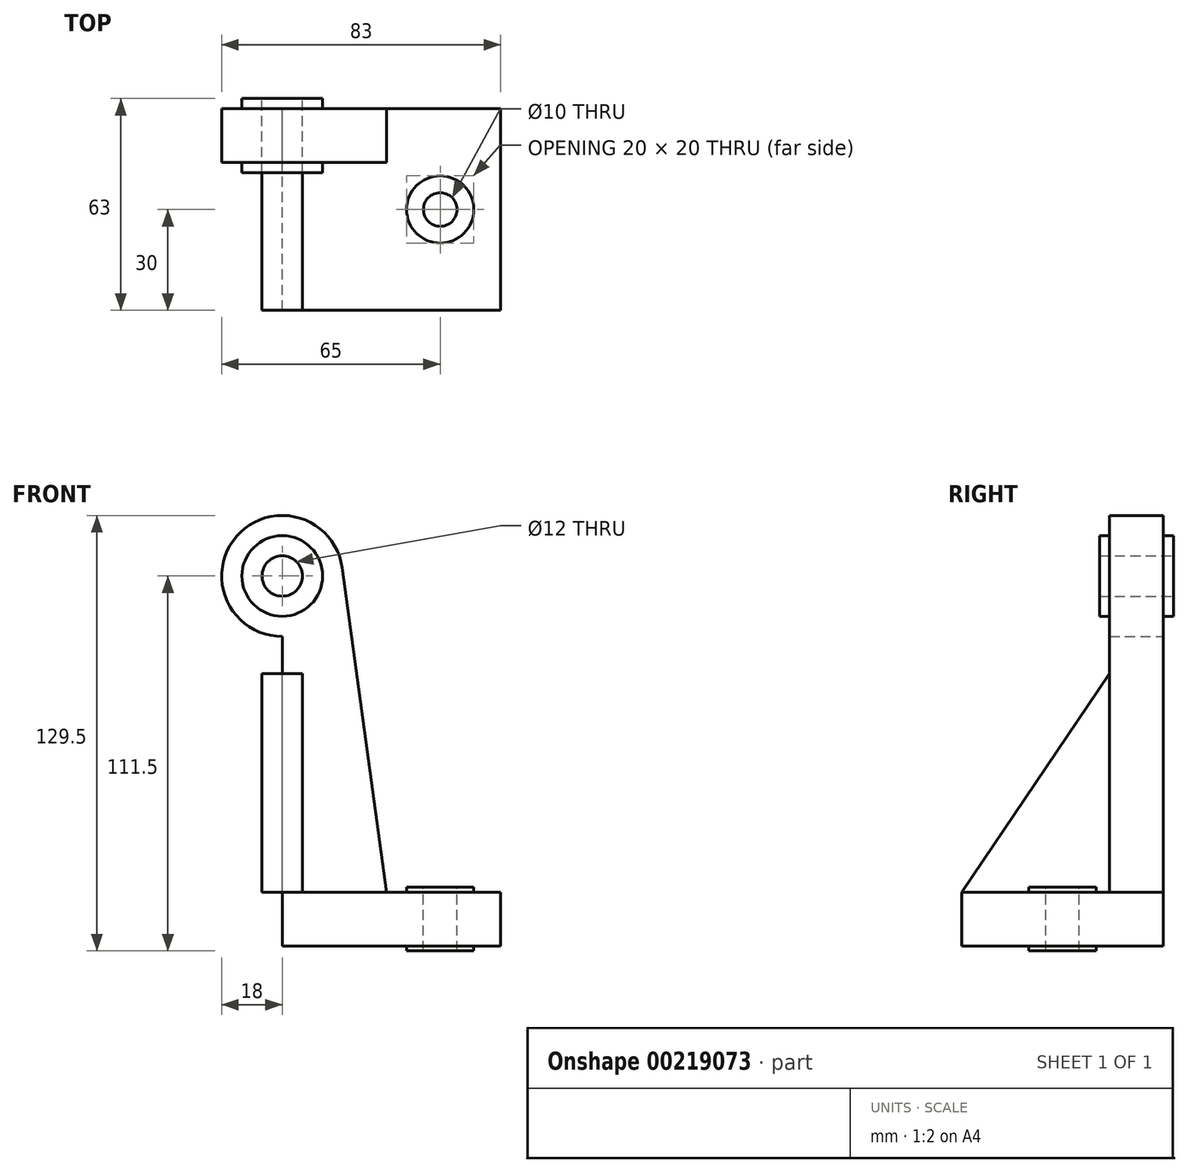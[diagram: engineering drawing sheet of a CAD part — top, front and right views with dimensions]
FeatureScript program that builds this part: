
annotation { "Feature Type Name" : "Feature", "Feature Type Description" : "" }
export const myFeature = defineFeature(function(context is Context, id is Id, definition is map)
    precondition{}
    {
        {
            var Q0;
            Q0=qCreatedBy(makeId("Front.planeOp"),FACE);
            var sketch = newSketch(context, id + "F0", { "sketchPlane" : qUnion([Q0])});
            skLineSegment(sketch, "E0.bottom", {"start": v(65, 0) * mm, "end": v(0, 0) * mm});
            skLineSegment(sketch, "E0.top", {"start": v(65, 16) * mm, "end": v(0, 16) * mm});
            skLineSegment(sketch, "E0.left", {"start": v(65, 0) * mm, "end": v(65, 16) * mm});
            skLineSegment(sketch, "E0.right", {"start": v(0, 0) * mm, "end": v(0, 16) * mm});
            skPoint(sketch, "E0.middle", {"position": v(32.5, 8) * mm});
            skLineSegment(sketch, "E1", {"start": v(0, 16) * mm, "end": v(0, 110) * mm});
            skCircle(sketch, "E2", {"center": v(0, 110) * mm, "radius": 12 * mm});
            skCircle(sketch, "E3", {"center": v(0, 110) * mm, "radius": 18 * mm});
            skCircle(sketch, "E4", {"center": v(0, 110) * mm, "radius": 6 * mm});
            skLineSegment(sketch, "E5", {"start": v(17.83, 112.43) * mm, "end": v(31, 16) * mm});
            skLineSegment(sketch, "E6", {"start": v(0, 110) * mm, "end": v(0, 128) * mm});
            skSolve(sketch);
        }
        {
            var Q0;
            Q0=makeQuery(id+"F0.imprint","IMPRINT",FACE,{"disambiguationData":[TD([[makeQuery(id+"F0.imprint","IMPRINT",EDGE,{"derivedFrom":sQuery(id+"F0.wireOp",EDGE,"E0.bottom")}),-1.0]])]});
            extrude(context, id + "F1", {"entities" : qUnion([Q0]), "depth" : 60 * mm});
        }
        {
            var Q0;
            {var subQ3=sQuery(id+"F0.wireOp",EDGE,"E5");Q0=makeQuery(id+"F0.imprint","IMPRINT",FACE,{"disambiguationData":[TD([[makeQuery(id+"F0.imprint","IMPRINT",EDGE,{"derivedFrom":subQ3}),-1.0]])]});}
            var Q1;
            {var subQ0=sQuery(id+"F0.wireOp",EDGE,"E3");var subQ2=sQuery(id+"F0.wireOp",EDGE,"E1");var subQ3=makeQuery(id+"F0.imprint","INTERSECT",VERTEX,{"derivedFrom":[subQ2,subQ0]});Q1=makeQuery(id+"F0.imprint","IMPRINT",FACE,{"disambiguationData":[TD([[makeQuery(id+"F0.imprint","IMPRINT",EDGE,{"disambiguationData":[TD([[subQ3,-1.0]])],"derivedFrom":subQ2}),-1.0]])]});}
            var Q2;
            {var subQ0=sQuery(id+"F0.wireOp",EDGE,"E3");var subQ1=sQuery(id+"F0.wireOp",EDGE,"E1");var subQ2=makeQuery(id+"F0.imprint","INTERSECT",VERTEX,{"derivedFrom":[subQ1,subQ0]});Q2=makeQuery(id+"F0.imprint","IMPRINT",FACE,{"disambiguationData":[TD([[makeQuery(id+"F0.imprint","IMPRINT",EDGE,{"disambiguationData":[TD([[subQ2,-1.0]])],"derivedFrom":subQ1}),1.0]])]});}
            extrude(context, id + "F2", {"entities" : qUnion([Q0, Q1, Q2]), "operationType" : NewBodyOperationType.ADD, "depth" : 16 * mm});
        }
        {
            var Q0;
            {var subQ0=sQuery(id+"F0.wireOp",EDGE,"E2");var subQ1=sQuery(id+"F0.wireOp",EDGE,"E1");var subQ2=makeQuery(id+"F0.imprint","INTERSECT",VERTEX,{"derivedFrom":[subQ1,subQ0]});Q0=makeQuery(id+"F0.imprint","IMPRINT",FACE,{"disambiguationData":[TD([[makeQuery(id+"F0.imprint","IMPRINT",EDGE,{"disambiguationData":[TD([[subQ2,-1.0]])],"derivedFrom":subQ1}),1.0]])]});}
            var Q1;
            {var subQ0=sQuery(id+"F0.wireOp",EDGE,"E2");var subQ1=sQuery(id+"F0.wireOp",EDGE,"E1");var subQ2=makeQuery(id+"F0.imprint","INTERSECT",VERTEX,{"derivedFrom":[subQ1,subQ0]});Q1=makeQuery(id+"F0.imprint","IMPRINT",FACE,{"disambiguationData":[TD([[makeQuery(id+"F0.imprint","IMPRINT",EDGE,{"disambiguationData":[TD([[subQ2,-1.0]])],"derivedFrom":subQ1}),-1.0]])]});}
            extrude(context, id + "F3", {"entities" : qUnion([Q0, Q1]), "operationType" : NewBodyOperationType.ADD, "depth" : 19 * mm});
        }
        {
            var Q0;
            {var subQ0=sQuery(id+"F0.wireOp",EDGE,"E2");var subQ1=sQuery(id+"F0.wireOp",EDGE,"E1");var subQ2=makeQuery(id+"F0.imprint","INTERSECT",VERTEX,{"derivedFrom":[subQ1,subQ0]});Q0=makeQuery(id+"F0.imprint","IMPRINT",FACE,{"disambiguationData":[TD([[makeQuery(id+"F0.imprint","IMPRINT",EDGE,{"disambiguationData":[TD([[subQ2,-1.0]])],"derivedFrom":subQ1}),1.0]])]});}
            var Q1;
            {var subQ0=sQuery(id+"F0.wireOp",EDGE,"E2");var subQ1=sQuery(id+"F0.wireOp",EDGE,"E1");var subQ2=makeQuery(id+"F0.imprint","INTERSECT",VERTEX,{"derivedFrom":[subQ1,subQ0]});Q1=makeQuery(id+"F0.imprint","IMPRINT",FACE,{"disambiguationData":[TD([[makeQuery(id+"F0.imprint","IMPRINT",EDGE,{"disambiguationData":[TD([[subQ2,-1.0]])],"derivedFrom":subQ1}),-1.0]])]});}
            extrude(context, id + "F4", {"entities" : qUnion([Q0, Q1]), "operationType" : NewBodyOperationType.ADD, "oppositeDirection" : true, "depth" : 3 * mm});
        }
        {
            var Q0;
            Q0=qCreatedBy(makeId("Right.planeOp"),FACE);
            var sketch = newSketch(context, id + "F5", { "sketchPlane" : qUnion([Q0])});
            skLineSegment(sketch, "E7.0", {"start": v(-16, 16) * mm, "end": v(-16, 92) * mm});
            skLineSegment(sketch, "E8.0", {"start": v(-60, 16) * mm, "end": v(-16, 16) * mm});
            skLineSegment(sketch, "E9", {"start": v(-60, 16) * mm, "end": v(-16, 81) * mm});
            skLineSegment(sketch, "E10.bottom", {"start": v(-50, 4) * mm, "end": v(-10, 4) * mm});
            skLineSegment(sketch, "E10.top", {"start": v(-50, 0) * mm, "end": v(-10, 0) * mm});
            skLineSegment(sketch, "E10.left", {"start": v(-50, 4) * mm, "end": v(-50, 0) * mm});
            skLineSegment(sketch, "E10.right", {"start": v(-10, 4) * mm, "end": v(-10, 0) * mm});
            skSolve(sketch);
        }
        {
            var Q0;
            {var subQ0=sQuery(id+"F5.wireOp",EDGE,"E8.0");Q0=makeQuery(id+"F5.imprint","IMPRINT",FACE,{"disambiguationData":[TD([[makeQuery(id+"F5.imprint","IMPRINT",EDGE,{"derivedFrom":subQ0}),1.0]])]});}
            extrude(context, id + "F6", {"entities" : qUnion([Q0]), "operationType" : NewBodyOperationType.ADD, "endBound" : BoundingType.SYMMETRIC, "depth" : 12 * mm});
        }
        {
            var Q0;
            Q0=makeQuery(id+"F1.opExtrude","SWEPT_FACE",FACE,{"disambiguationData":[OSD([sQuery(id+"F0.wireOp",EDGE,"E0.top")])]});
            var sketch = newSketch(context, id + "F7", { "sketchPlane" : qUnion([Q0])});
            skCircle(sketch, "E11", {"center": v(47, -30) * mm, "radius": 10 * mm});
            skCircle(sketch, "E12", {"center": v(47, -30) * mm, "radius": 5 * mm});
            skSolve(sketch);
        }
        {
            var Q0;
            Q0=makeQuery(id+"F7.imprint","IMPRINT",FACE,{"disambiguationData":[TD([[makeQuery(id+"F7.imprint","IMPRINT",EDGE,{"derivedFrom":sQuery(id+"F7.wireOp",EDGE,"E11")}),1.0]])]});
            extrude(context, id + "F8", {"entities" : qUnion([Q0]), "operationType" : NewBodyOperationType.ADD, "endBound" : BoundingType.SYMMETRIC, "oppositeDirection" : true, "depth" : 3 * mm});
        }
        {
            var Q0;
            Q0=makeQuery(id+"F8.boolean.opBoolean","SPLIT",FACE,{"disambiguationData":[TD([makeQuery(id+"F8.opExtrude","SWEPT_FACE",FACE,{"disambiguationData":[OSD([sQuery(id+"F7.wireOp",EDGE,"E12")])]})])],"derivedFrom":makeQuery(id+"F1.opExtrude","SWEPT_FACE",FACE,{"disambiguationData":[OSD([sQuery(id+"F0.wireOp",EDGE,"E0.top")])]})});
            extrude(context, id + "F9", {"entities" : qUnion([Q0]), "operationType" : NewBodyOperationType.REMOVE, "endBound" : BoundingType.UP_TO_NEXT, "oppositeDirection" : true, "depth" : 25 * mm});
        }
        {
            var Q0;
            Q0=makeQuery(id+"F8.opExtrude","CAP_FACE",FACE,{"disambiguationData":[OSD([sQuery(id+"F7.wireOp",EDGE,"E11"),sQuery(id+"F7.wireOp",EDGE,"E12")])],"isStart":true});
            extrude(context, id + "F10", {"entities" : qUnion([Q0]), "operationType" : NewBodyOperationType.ADD, "oppositeDirection" : true, "depth" : 19 * mm});
        }
    });
